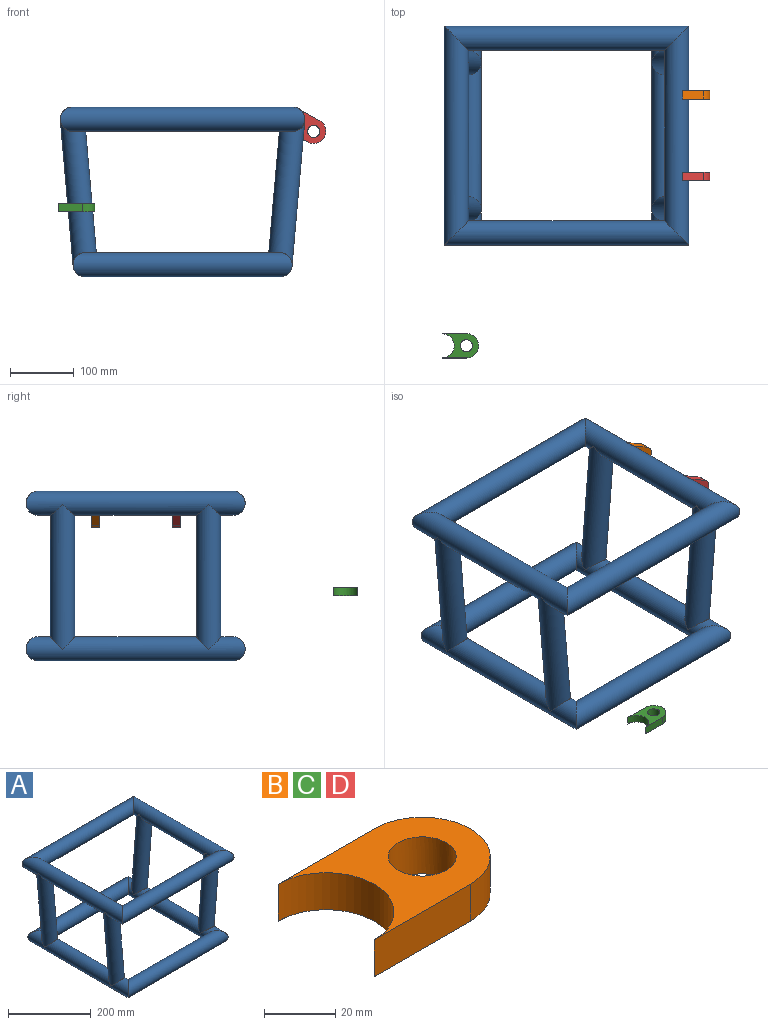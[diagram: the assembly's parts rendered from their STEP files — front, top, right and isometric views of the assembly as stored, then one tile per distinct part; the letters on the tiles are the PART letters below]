
ASSEMBLY  parts=4 mates=1
PART A: 32 faces, bbox 383.3x343.2x265.8 mm
  f0: cylinder r=19.05mm len=343.16mm, axis (0,-1,0), area 33579.7mm2, adj f2,f3,f9,f10
  f1: cylinder r=19.05mm len=343.16mm, axis (0,1,0), area 33579.7mm2, adj f2,f3,f8,f11
  f2: cylinder r=19.05mm len=343.42mm, axis (1,0,0), area 36482.9mm2, adj f0,f1
  f3: cylinder r=19.05mm len=342.9mm, axis (-1,0,0), area 36482.9mm2, adj f0,f1
  f4: cylinder r=19.05mm len=343.16mm, axis (0,1,0), area 33579.7mm2, adj f6,f7,f8,f11
  f5: cylinder r=19.05mm len=343.16mm, axis (0,-1,0), area 33579.7mm2, adj f6,f7,f9,f10
  f6: cylinder r=19.05mm len=383.27mm, axis (1,0,0), area 41252.4mm2, adj f4,f5
  f7: cylinder r=19.05mm len=382.75mm, axis (-1,0,0), area 41252.5mm2, adj f4,f5
  f8: cylinder r=19.05mm len=231.05mm, axis (0.09,0,1), area 24459mm2, adj f1,f4
  f9: cylinder r=19.05mm len=231.05mm, axis (-0.09,0,1), area 24459mm2, adj f0,f5
  f10: cylinder r=19.05mm len=231.05mm, axis (-0.09,0,1), area 24459mm2, adj f0,f5
  f11: cylinder r=19.05mm len=231.05mm, axis (0.09,0,1), area 24459mm2, adj f1,f4
  f12: cylinder r=19.05mm len=32.01mm, axis (0,-1,0), area 906.4mm2, adj f13
  f13: cylinder r=16mm len=209.93mm, axis (-0.09,0,1), area 19963.8mm2, adj f12,f14
  f14: cylinder r=19.05mm len=32.01mm, axis (0,-1,0), area 907.3mm2, adj f13
  f15: cylinder r=19.05mm len=32.01mm, axis (0,-1,0), area 906.4mm2, adj f16
  f16: cylinder r=16mm len=209.93mm, axis (-0.09,0,1), area 19963.8mm2, adj f15,f17
  f17: cylinder r=19.05mm len=32.01mm, axis (0,-1,0), area 907.3mm2, adj f16
  f18: cylinder r=19.05mm len=32.01mm, axis (0,1,0), area 906.4mm2, adj f19
  f19: cylinder r=16mm len=209.93mm, axis (0.09,0,1), area 19963.8mm2, adj f18,f20
  f20: cylinder r=19.05mm len=32.01mm, axis (0,1,0), area 907.3mm2, adj f19
  f21: cylinder r=19.05mm len=32.01mm, axis (0,1,0), area 906.4mm2, adj f22
  f22: cylinder r=16mm len=209.93mm, axis (0.09,0,1), area 19963.8mm2, adj f21,f23
  f23: cylinder r=19.05mm len=32.01mm, axis (0,1,0), area 907.3mm2, adj f22
  f24: cylinder r=16mm len=337.02mm, axis (0,-1,0), area 30645.6mm2, adj f25,f26
  f25: cylinder r=16mm len=337.24mm, axis (1,0,0), area 30645.6mm2, adj f24,f27
  f26: cylinder r=16mm len=336.8mm, axis (-1,0,0), area 30645.7mm2, adj f24,f27
  f27: cylinder r=16mm len=337.02mm, axis (0,1,0), area 30645.6mm2, adj f25,f26
  f28: cylinder r=16mm len=337.02mm, axis (0,-1,0), area 30645.6mm2, adj f29,f30
  f29: cylinder r=16mm len=377.09mm, axis (1,0,0), area 34652mm2, adj f28,f31
  f30: cylinder r=16mm len=376.65mm, axis (-1,0,0), area 34652.1mm2, adj f28,f31
  f31: cylinder r=16mm len=337.02mm, axis (0,1,0), area 30645.6mm2, adj f29,f30
PART B: 7 faces, bbox 57.2x38.1x12.7 mm
  f0: plane 38.1x12.7mm, normal (0,1,0), area 483.9mm2, adj f1,f3,f4,f5
  f1: cylinder r=19.05mm len=38.1mm, axis (0,0,-1), area 760.1mm2, adj f0,f2,f4,f5
  f2: plane 38.1x12.7mm, normal (0,-1,0), area 483.9mm2, adj f1,f3,f4,f5
  f3: cylinder r=19.05mm len=38.1mm, axis (0,0,-1), area 760.1mm2, adj f0,f2,f4,f5
  f4: plane 57.15x38.1mm, normal (0,0,1), area 1166.6mm2, adj f0,f1,f2,f3,f6
  f5: plane 57.15x38.1mm, normal (0,0,-1), area 1166.6mm2, adj f0,f1,f2,f3,f6
  f6: cylinder r=9.53mm len=19.05mm, axis (0,0,-1), area 760.1mm2, adj f4,f5
PART C: same geometry as B
PART D: same geometry as B
PLACE A t=(-47.42,-7.87,104.72)mm fixed
PLACE B rot(axis=(0.94,0.25,-0.25),93.8deg) t=(124.9,61.98,332.45)mm
PLACE C t=(-242.23,-336.68,187.62)mm
PLACE D rot(axis=(0.94,0.25,-0.25),93.8deg) t=(124.9,-65.02,332.45)mm
MATE fastened B.f1 <-> A.f4  axis (0,1,0) through (124.9,55.63,332.45)mm
